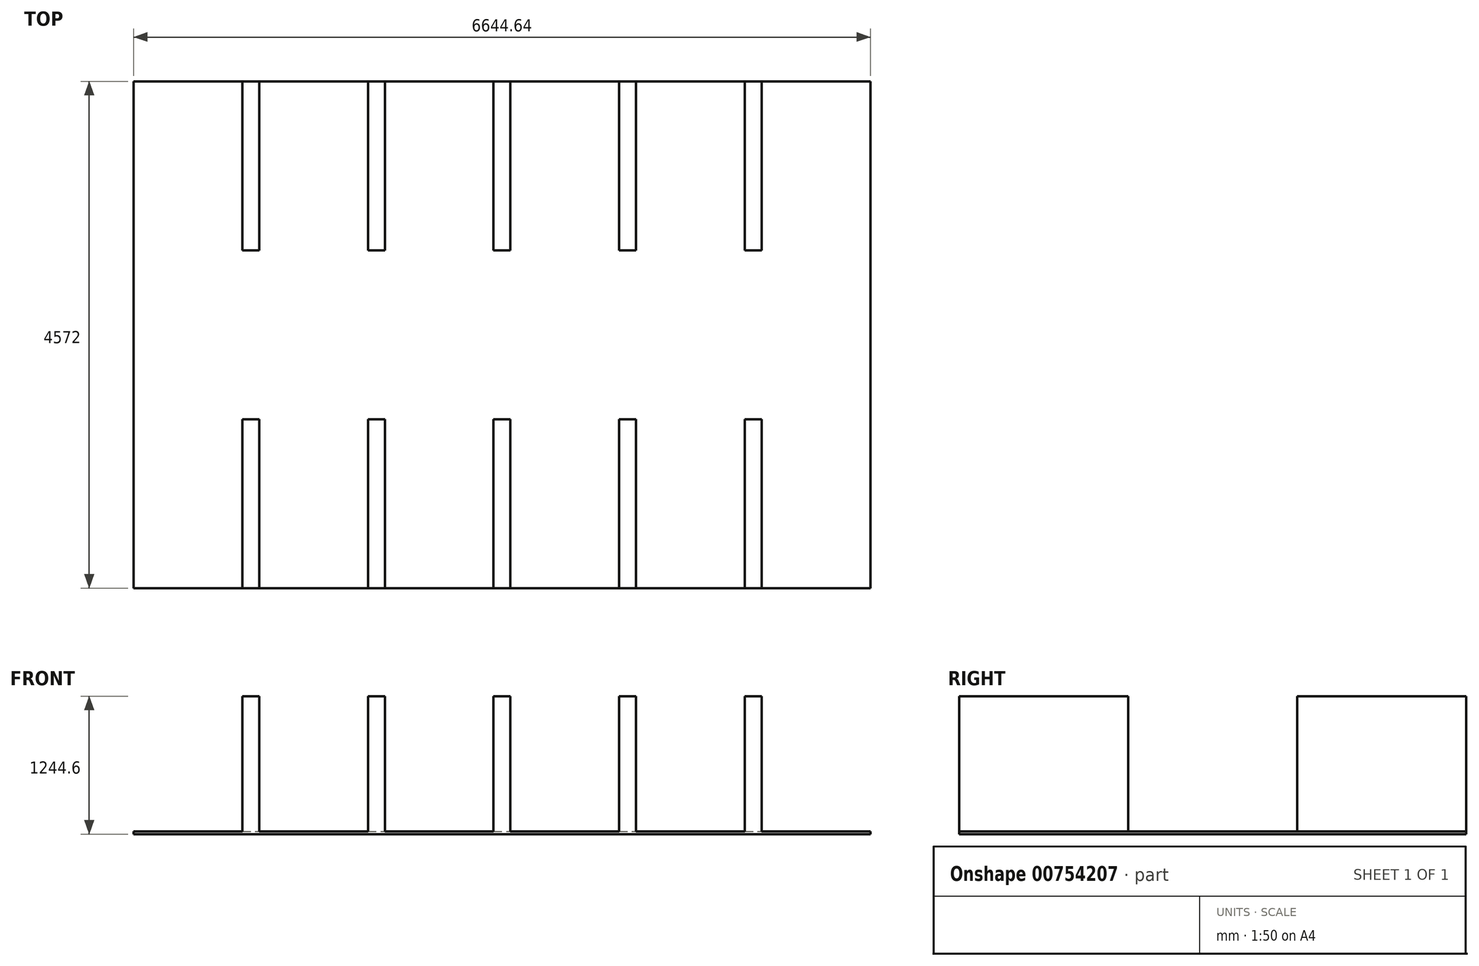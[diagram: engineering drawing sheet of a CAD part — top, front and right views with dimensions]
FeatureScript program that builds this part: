
annotation { "Feature Type Name" : "Feature", "Feature Type Description" : "" }
export const myFeature = defineFeature(function(context is Context, id is Id, definition is map)
    precondition{}
    {
        {
            var Q0;
            Q0=qCreatedBy(makeId("Top.planeOp"),FACE);
            var sketch = newSketch(context, id + "F0", { "sketchPlane" : qUnion([Q0])});
            skLineSegment(sketch, "E0.bottom", {"start": v(-3322.32, 2286) * mm, "end": v(3322.32, 2286) * mm});
            skLineSegment(sketch, "E0.top", {"start": v(-3322.32, -2286) * mm, "end": v(3322.32, -2286) * mm});
            skLineSegment(sketch, "E0.left", {"start": v(-3322.32, 2286) * mm, "end": v(-3322.32, -2286) * mm});
            skLineSegment(sketch, "E0.right", {"start": v(3322.32, 2286) * mm, "end": v(3322.32, -2286) * mm});
            skPoint(sketch, "E0.middle", {"position": v(0, 0) * mm});
            skLineSegment(sketch, "E1", {"start": v(-2341.88, 2286) * mm, "end": v(-2341.88, 762) * mm});
            skLineSegment(sketch, "E2", {"start": v(-3322.32, 762) * mm, "end": v(-2993.8, 762) * mm});
            skLineSegment(sketch, "E3", {"start": v(-3322.32, -762) * mm, "end": v(-2341.88, -762) * mm});
            skLineSegment(sketch, "E4", {"start": v(-2189.48, 2286) * mm, "end": v(-2189.48, 762) * mm});
            skLineSegment(sketch, "E5", {"start": v(-1209.04, 2286) * mm, "end": v(-1209.04, 762) * mm});
            skLineSegment(sketch, "E6", {"start": v(-1056.64, 2286) * mm, "end": v(-1056.64, 762) * mm});
            skLineSegment(sketch, "E7", {"start": v(-76.2, 2286) * mm, "end": v(-76.2, 762) * mm});
            skLineSegment(sketch, "E8", {"start": v(76.2, 2286) * mm, "end": v(76.2, 762) * mm});
            skLineSegment(sketch, "E9", {"start": v(1056.64, 2286) * mm, "end": v(1056.64, 762) * mm});
            skLineSegment(sketch, "E10", {"start": v(1209.04, 2286) * mm, "end": v(1209.04, 762) * mm});
            skLineSegment(sketch, "E11", {"start": v(2189.48, 2286) * mm, "end": v(2189.48, 762) * mm});
            skLineSegment(sketch, "E12", {"start": v(2341.88, 2286) * mm, "end": v(2341.88, 762) * mm});
            skLineSegment(sketch, "E13", {"start": v(-2993.8, 762) * mm, "end": v(3322.32, 762) * mm});
            skLineSegment(sketch, "E14", {"start": v(-2341.88, -762) * mm, "end": v(-2189.48, -762) * mm});
            skLineSegment(sketch, "E15", {"start": v(-2189.48, -762) * mm, "end": v(-1209.04, -762) * mm});
            skLineSegment(sketch, "E16", {"start": v(-1209.04, -762) * mm, "end": v(-1056.64, -762) * mm});
            skLineSegment(sketch, "E17", {"start": v(-1056.64, -762) * mm, "end": v(-76.2, -762) * mm});
            skLineSegment(sketch, "E18", {"start": v(-76.2, -762) * mm, "end": v(76.2, -762) * mm});
            skLineSegment(sketch, "E19", {"start": v(76.2, -762) * mm, "end": v(1056.64, -762) * mm});
            skLineSegment(sketch, "E20", {"start": v(1056.64, -762) * mm, "end": v(1209.04, -762) * mm});
            skLineSegment(sketch, "E21", {"start": v(1209.04, -762) * mm, "end": v(2189.48, -762) * mm});
            skLineSegment(sketch, "E22", {"start": v(2189.48, -762) * mm, "end": v(2341.88, -762) * mm});
            skLineSegment(sketch, "E23", {"start": v(2341.88, -762) * mm, "end": v(3322.32, -762) * mm});
            skLineSegment(sketch, "E24.trimOffspring", {"start": v(-2189.48, -762) * mm, "end": v(-2189.48, -2286) * mm});
            skLineSegment(sketch, "E25.trimOffspring", {"start": v(-2341.88, -762) * mm, "end": v(-2341.88, -2286) * mm});
            skLineSegment(sketch, "E26.trimOffspring", {"start": v(-1209.04, -762) * mm, "end": v(-1209.04, -2286) * mm});
            skLineSegment(sketch, "E27.trimOffspring", {"start": v(-1056.64, -762) * mm, "end": v(-1056.64, -2286) * mm});
            skLineSegment(sketch, "E28.trimOffspring", {"start": v(-76.2, -762) * mm, "end": v(-76.2, -2286) * mm});
            skLineSegment(sketch, "E29.trimOffspring", {"start": v(76.2, -762) * mm, "end": v(76.2, -2286) * mm});
            skLineSegment(sketch, "E30.trimOffspring", {"start": v(1056.64, -762) * mm, "end": v(1056.64, -2286) * mm});
            skLineSegment(sketch, "E31.trimOffspring", {"start": v(1209.04, -762) * mm, "end": v(1209.04, -2286) * mm});
            skLineSegment(sketch, "E32.trimOffspring", {"start": v(2189.48, -762) * mm, "end": v(2189.48, -2286) * mm});
            skLineSegment(sketch, "E33.trimOffspring", {"start": v(2341.88, -762) * mm, "end": v(2341.88, -2286) * mm});
            skSolve(sketch);
        }
        {
            var Q0;
            {var subQ10=sQuery(id+"F0.wireOp",EDGE,"E2");Q0=makeQuery(id+"F0.imprint","IMPRINT",FACE,{"disambiguationData":[TD([[makeQuery(id+"F0.imprint","IMPRINT",EDGE,{"derivedFrom":subQ10}),-1.0]])]});}
            var Q1;
            {var subQ4=sQuery(id+"F0.wireOp",EDGE,"E3");Q1=makeQuery(id+"F0.imprint","IMPRINT",FACE,{"disambiguationData":[TD([[makeQuery(id+"F0.imprint","IMPRINT",EDGE,{"derivedFrom":subQ4}),-1.0]])]});}
            var Q2;
            Q2=makeQuery(id+"F0.imprint","IMPRINT",FACE,{"disambiguationData":[TD([[makeQuery(id+"F0.imprint","IMPRINT",EDGE,{"derivedFrom":sQuery(id+"F0.wireOp",EDGE,"E14")}),-1.0]])]});
            var Q3;
            Q3=makeQuery(id+"F0.imprint","IMPRINT",FACE,{"disambiguationData":[TD([[makeQuery(id+"F0.imprint","IMPRINT",EDGE,{"derivedFrom":sQuery(id+"F0.wireOp",EDGE,"E16")}),-1.0]])]});
            var Q4;
            Q4=makeQuery(id+"F0.imprint","IMPRINT",FACE,{"disambiguationData":[TD([[makeQuery(id+"F0.imprint","IMPRINT",EDGE,{"derivedFrom":sQuery(id+"F0.wireOp",EDGE,"E17")}),-1.0]])]});
            var Q5;
            Q5=makeQuery(id+"F0.imprint","IMPRINT",FACE,{"disambiguationData":[TD([[makeQuery(id+"F0.imprint","IMPRINT",EDGE,{"derivedFrom":sQuery(id+"F0.wireOp",EDGE,"E19")}),-1.0]])]});
            var Q6;
            Q6=makeQuery(id+"F0.imprint","IMPRINT",FACE,{"disambiguationData":[TD([[makeQuery(id+"F0.imprint","IMPRINT",EDGE,{"derivedFrom":sQuery(id+"F0.wireOp",EDGE,"E21")}),-1.0]])]});
            var Q7;
            {var subQ4=sQuery(id+"F0.wireOp",EDGE,"E23");Q7=makeQuery(id+"F0.imprint","IMPRINT",FACE,{"disambiguationData":[TD([[makeQuery(id+"F0.imprint","IMPRINT",EDGE,{"derivedFrom":subQ4}),-1.0]])]});}
            var Q8;
            {var subQ3=sQuery(id+"F0.wireOp",EDGE,"E12");Q8=makeQuery(id+"F0.imprint","IMPRINT",FACE,{"disambiguationData":[TD([[makeQuery(id+"F0.imprint","IMPRINT",EDGE,{"derivedFrom":subQ3}),1.0]])]});}
            var Q9;
            {var subQ0=sQuery(id+"F0.wireOp",EDGE,"E11");Q9=makeQuery(id+"F0.imprint","IMPRINT",FACE,{"disambiguationData":[TD([[makeQuery(id+"F0.imprint","IMPRINT",EDGE,{"derivedFrom":subQ0}),1.0]])]});}
            var Q10;
            {var subQ0=sQuery(id+"F0.wireOp",EDGE,"E10");Q10=makeQuery(id+"F0.imprint","IMPRINT",FACE,{"disambiguationData":[TD([[makeQuery(id+"F0.imprint","IMPRINT",EDGE,{"derivedFrom":subQ0}),1.0]])]});}
            var Q11;
            {var subQ0=sQuery(id+"F0.wireOp",EDGE,"E6");Q11=makeQuery(id+"F0.imprint","IMPRINT",FACE,{"disambiguationData":[TD([[makeQuery(id+"F0.imprint","IMPRINT",EDGE,{"derivedFrom":subQ0}),1.0]])]});}
            var Q12;
            {var subQ0=sQuery(id+"F0.wireOp",EDGE,"E4");Q12=makeQuery(id+"F0.imprint","IMPRINT",FACE,{"disambiguationData":[TD([[makeQuery(id+"F0.imprint","IMPRINT",EDGE,{"derivedFrom":subQ0}),1.0]])]});}
            var Q13;
            {var subQ2=sQuery(id+"F0.wireOp",EDGE,"E1");Q13=makeQuery(id+"F0.imprint","IMPRINT",FACE,{"disambiguationData":[TD([[makeQuery(id+"F0.imprint","IMPRINT",EDGE,{"derivedFrom":subQ2}),-1.0]])]});}
            var Q14;
            {var subQ0=sQuery(id+"F0.wireOp",EDGE,"E5");Q14=makeQuery(id+"F0.imprint","IMPRINT",FACE,{"disambiguationData":[TD([[makeQuery(id+"F0.imprint","IMPRINT",EDGE,{"derivedFrom":subQ0}),1.0]])]});}
            var Q15;
            {var subQ0=sQuery(id+"F0.wireOp",EDGE,"E1");Q15=makeQuery(id+"F0.imprint","IMPRINT",FACE,{"disambiguationData":[TD([[makeQuery(id+"F0.imprint","IMPRINT",EDGE,{"derivedFrom":subQ0}),1.0]])]});}
            var Q16;
            {var subQ0=sQuery(id+"F0.wireOp",EDGE,"E7");Q16=makeQuery(id+"F0.imprint","IMPRINT",FACE,{"disambiguationData":[TD([[makeQuery(id+"F0.imprint","IMPRINT",EDGE,{"derivedFrom":subQ0}),1.0]])]});}
            var Q17;
            Q17=makeQuery(id+"F0.imprint","IMPRINT",FACE,{"disambiguationData":[TD([[makeQuery(id+"F0.imprint","IMPRINT",EDGE,{"derivedFrom":sQuery(id+"F0.wireOp",EDGE,"E20")}),-1.0]])]});
            var Q18;
            {var subQ0=sQuery(id+"F0.wireOp",EDGE,"E8");Q18=makeQuery(id+"F0.imprint","IMPRINT",FACE,{"disambiguationData":[TD([[makeQuery(id+"F0.imprint","IMPRINT",EDGE,{"derivedFrom":subQ0}),1.0]])]});}
            var Q19;
            {var subQ0=sQuery(id+"F0.wireOp",EDGE,"E9");Q19=makeQuery(id+"F0.imprint","IMPRINT",FACE,{"disambiguationData":[TD([[makeQuery(id+"F0.imprint","IMPRINT",EDGE,{"derivedFrom":subQ0}),1.0]])]});}
            var Q20;
            Q20=makeQuery(id+"F0.imprint","IMPRINT",FACE,{"disambiguationData":[TD([[makeQuery(id+"F0.imprint","IMPRINT",EDGE,{"derivedFrom":sQuery(id+"F0.wireOp",EDGE,"E22")}),-1.0]])]});
            var Q21;
            Q21=makeQuery(id+"F0.imprint","IMPRINT",FACE,{"disambiguationData":[TD([[makeQuery(id+"F0.imprint","IMPRINT",EDGE,{"derivedFrom":sQuery(id+"F0.wireOp",EDGE,"E18")}),-1.0]])]});
            var Q22;
            Q22=makeQuery(id+"F0.imprint","IMPRINT",FACE,{"disambiguationData":[TD([[makeQuery(id+"F0.imprint","IMPRINT",EDGE,{"derivedFrom":sQuery(id+"F0.wireOp",EDGE,"E15")}),-1.0]])]});
            extrude(context, id + "F1", {"entities" : qUnion([Q0, Q1, Q2, Q3, Q4, Q5, Q6, Q7, Q8, Q9, Q10, Q11, Q12, Q13, Q14, Q15, Q16, Q17, Q18, Q19, Q20, Q21, Q22]), "oppositeDirection" : true, "depth" : 25.4 * mm, "offsetDistance" : 25.4 * mm});
        }
        {
            var Q0;
            Q0=makeQuery(id+"F0.imprint","IMPRINT",FACE,{"disambiguationData":[TD([[makeQuery(id+"F0.imprint","IMPRINT",EDGE,{"derivedFrom":sQuery(id+"F0.wireOp",EDGE,"E14")}),-1.0]])]});
            var Q1;
            {var subQ0=sQuery(id+"F0.wireOp",EDGE,"E1");Q1=makeQuery(id+"F0.imprint","IMPRINT",FACE,{"disambiguationData":[TD([[makeQuery(id+"F0.imprint","IMPRINT",EDGE,{"derivedFrom":subQ0}),1.0]])]});}
            var Q2;
            Q2=makeQuery(id+"F0.imprint","IMPRINT",FACE,{"disambiguationData":[TD([[makeQuery(id+"F0.imprint","IMPRINT",EDGE,{"derivedFrom":sQuery(id+"F0.wireOp",EDGE,"E16")}),-1.0]])]});
            var Q3;
            {var subQ0=sQuery(id+"F0.wireOp",EDGE,"E5");Q3=makeQuery(id+"F0.imprint","IMPRINT",FACE,{"disambiguationData":[TD([[makeQuery(id+"F0.imprint","IMPRINT",EDGE,{"derivedFrom":subQ0}),1.0]])]});}
            var Q4;
            Q4=makeQuery(id+"F0.imprint","IMPRINT",FACE,{"disambiguationData":[TD([[makeQuery(id+"F0.imprint","IMPRINT",EDGE,{"derivedFrom":sQuery(id+"F0.wireOp",EDGE,"E18")}),-1.0]])]});
            var Q5;
            {var subQ0=sQuery(id+"F0.wireOp",EDGE,"E7");Q5=makeQuery(id+"F0.imprint","IMPRINT",FACE,{"disambiguationData":[TD([[makeQuery(id+"F0.imprint","IMPRINT",EDGE,{"derivedFrom":subQ0}),1.0]])]});}
            var Q6;
            {var subQ0=sQuery(id+"F0.wireOp",EDGE,"E9");Q6=makeQuery(id+"F0.imprint","IMPRINT",FACE,{"disambiguationData":[TD([[makeQuery(id+"F0.imprint","IMPRINT",EDGE,{"derivedFrom":subQ0}),1.0]])]});}
            var Q7;
            Q7=makeQuery(id+"F0.imprint","IMPRINT",FACE,{"disambiguationData":[TD([[makeQuery(id+"F0.imprint","IMPRINT",EDGE,{"derivedFrom":sQuery(id+"F0.wireOp",EDGE,"E20")}),-1.0]])]});
            var Q8;
            Q8=makeQuery(id+"F0.imprint","IMPRINT",FACE,{"disambiguationData":[TD([[makeQuery(id+"F0.imprint","IMPRINT",EDGE,{"derivedFrom":sQuery(id+"F0.wireOp",EDGE,"E22")}),-1.0]])]});
            var Q9;
            {var subQ0=sQuery(id+"F0.wireOp",EDGE,"E11");Q9=makeQuery(id+"F0.imprint","IMPRINT",FACE,{"disambiguationData":[TD([[makeQuery(id+"F0.imprint","IMPRINT",EDGE,{"derivedFrom":subQ0}),1.0]])]});}
            extrude(context, id + "F2", {"entities" : qUnion([Q0, Q1, Q2, Q3, Q4, Q5, Q6, Q7, Q8, Q9]), "operationType" : NewBodyOperationType.ADD, "depth" : 1219.2 * mm, "offsetDistance" : 25.4 * mm});
        }
    });
